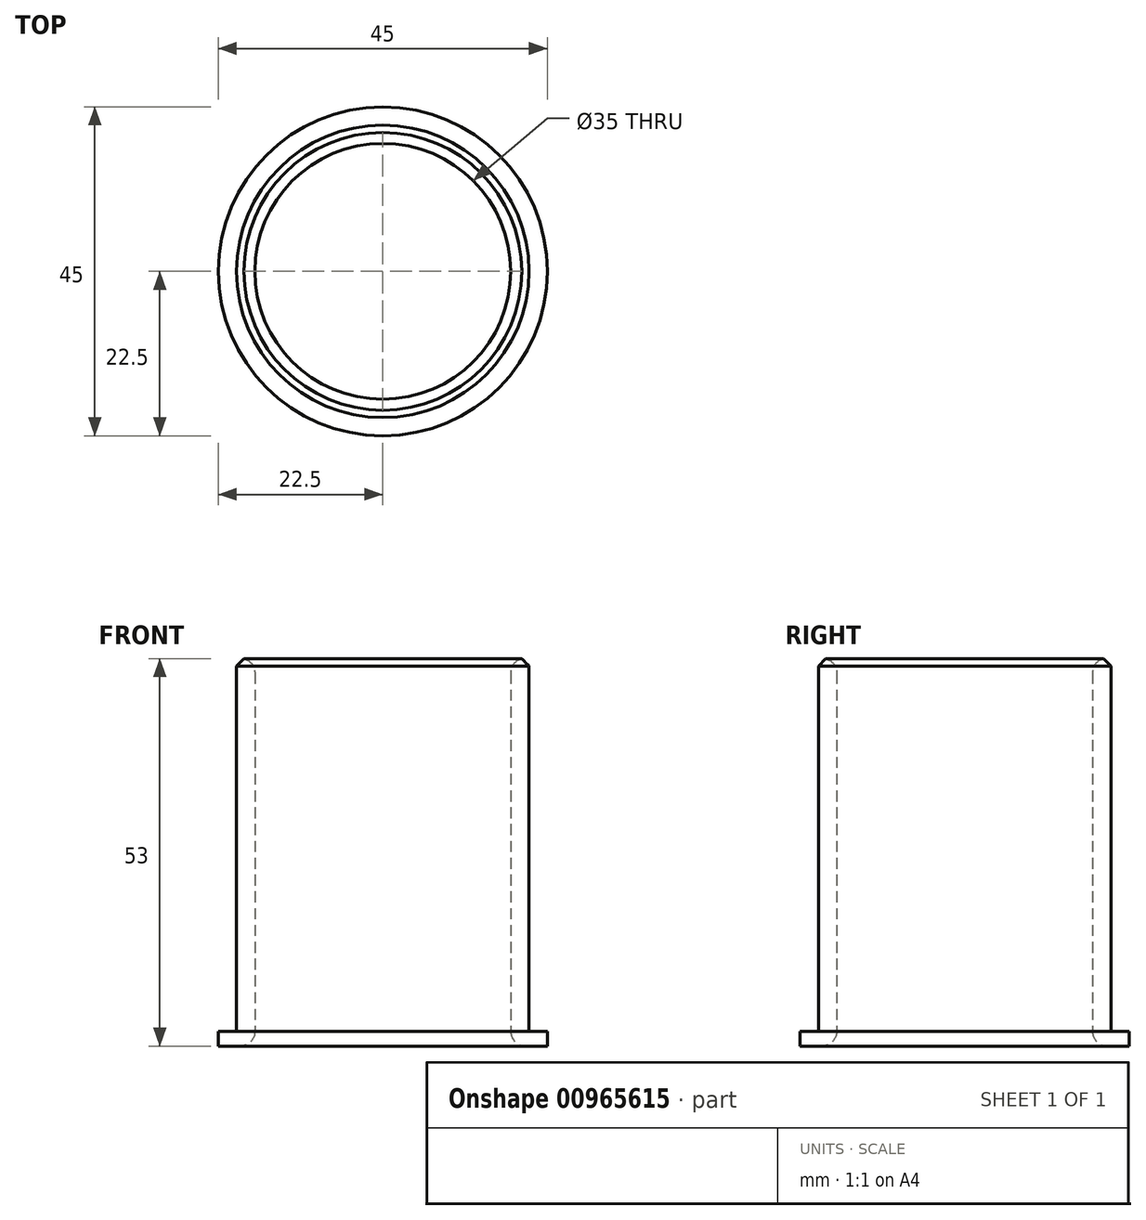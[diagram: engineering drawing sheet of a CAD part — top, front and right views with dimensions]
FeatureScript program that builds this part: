
annotation { "Feature Type Name" : "Feature", "Feature Type Description" : "" }
export const myFeature = defineFeature(function(context is Context, id is Id, definition is map)
    precondition{}
    {
        {
            var Q0;
            Q0=qCreatedBy(makeId("Top.planeOp"),FACE);
            var sketch = newSketch(context, id + "F0", { "sketchPlane" : qUnion([Q0])});
            skCircle(sketch, "E0", {"center": v(0, 0) * mm, "radius": 20 * mm});
            skCircle(sketch, "E1", {"center": v(0, 0) * mm, "radius": 22.5 * mm});
            skSolve(sketch);
        }
        {
            var Q0;
            Q0=makeQuery(id+"F0.imprint","IMPRINT",FACE,{"disambiguationData":[TD([[makeQuery(id+"F0.imprint","IMPRINT",EDGE,{"derivedFrom":sQuery(id+"F0.wireOp",EDGE,"E0")}),1.0]])]});
            extrude(context, id + "F1", {"entities" : qUnion([Q0]), "depth" : 53 * mm, "offsetDistance" : 25 * mm});
        }
        {
            var Q0;
            Q0 = qSketchRegion(id + "F0", true);
            extrude(context, id + "F2", {"entities" : qUnion([Q0]), "operationType" : NewBodyOperationType.ADD, "depth" : 2 * mm, "offsetDistance" : 25 * mm});
        }
        {
            var Q0;
            Q0=makeQuery(id+"F1.opExtrude","CAP_FACE",FACE,{"disambiguationData":[OSD([sQuery(id+"F0.wireOp",EDGE,"E0")])],"isStart":false});
            shell(context, id + "F3", {"entities" : qUnion([Q0]), "thickness" : 2.5 * mm});
        }
        {
            var Q0;
            Q0=makeQuery(id+"F3.opShell","OFFSET_FACE",FACE,{"disambiguationData":[OSD([sQuery(id+"F0.wireOp",EDGE,"E0"),sQuery(id+"F0.wireOp",EDGE,"E1")])]});
            extrude(context, id + "F4", {"entities" : qUnion([Q0]), "operationType" : NewBodyOperationType.REMOVE, "oppositeDirection" : true, "depth" : 3 * mm, "offsetDistance" : 25 * mm});
        }
        {
            var Q0;
            Q0=makeQuery(id+"F1.opExtrude","CAP_EDGE",EDGE,{"disambiguationData":[OSD([sQuery(id+"F0.wireOp",EDGE,"E0")])],"isStart":false});
            chamfer(context, id + "F5", {"entities" : qUnion([Q0]), "width" : 1 * mm, "tangentPropagation" : true});
        }
        {
            var Q0;
            Q0=makeQuery(id+"F3.opShell","OFFSET_EDGE",EDGE,{"disambiguationData":[OSD([sQuery(id+"F0.wireOp",EDGE,"E0")])]});
            fillet(context, id + "F6", {"entities" : qUnion([Q0]), "radius" : 2 * mm, "tangentPropagation" : true, "allowEdgeOverflow" : false});
        }
        {
            var Q0;
            {var subQ0=sQuery(id+"F0.wireOp",EDGE,"E1");var subQ1=sQuery(id+"F0.wireOp",EDGE,"E0");Q0=makeQuery(id+"F4.boolean.opBoolean","INTERSECT",EDGE,{"derivedFrom":[makeQuery(id+"F2.boolean.opBoolean","MERGE",FACE,{"derivedFrom":[makeQuery(id+"F1.opExtrude","CAP_FACE",FACE,{"disambiguationData":[OSD([subQ1])],"isStart":true}),makeQuery(id+"F2.opExtrude","CAP_FACE",FACE,{"disambiguationData":[OSD([subQ1,subQ0])],"isStart":true})]}),makeQuery(id+"F4.opExtrude","SWEPT_FACE",FACE,{"disambiguationData":[OSD([subQ1,subQ0])]})]});}
            fillet(context, id + "F7", {"entities" : qUnion([Q0]), "radius" : 2 * mm, "tangentPropagation" : true, "allowEdgeOverflow" : false});
        }
    });
